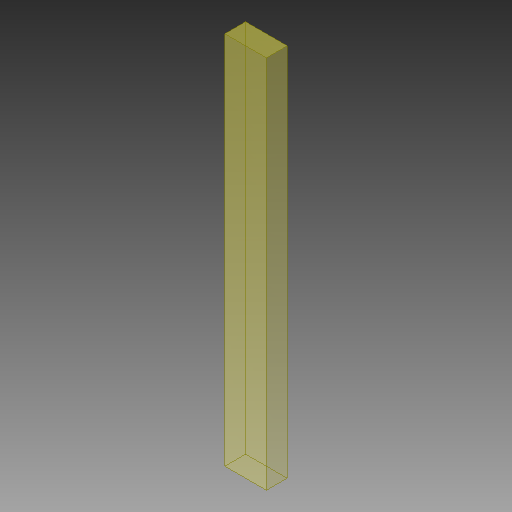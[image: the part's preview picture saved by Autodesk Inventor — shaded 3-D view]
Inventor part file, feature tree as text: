
AUTODESK INVENTOR PART (.ipt)
format: ipt  version: 2018.1 (Build 221171000, 171)  size: 109,056 bytes
history: native  units: mm
features: other x1, extrude x1, sketch x1
ambient origin geometry x8: Origin, YZ Plane, XZ Plane, XY Plane, X Axis, Y Axis, Z Axis, Center Point
bodies: Solid1 (feature_tree)
feature tree (3):
  parser-record x1  (decoder bookkeeping rows leaked as tree rows — omitted from the tree; the rows remain in map.json)
  extrude  "Extrusion1"  Depth=90.0mm
  sketch  "Sketch1"  dims[d0=10.0mm d1=90.0mm d2=5.0mm d3=0.0mm]
note: 1 file-system path scrubbed to <path> (originals preserved in map.json)
